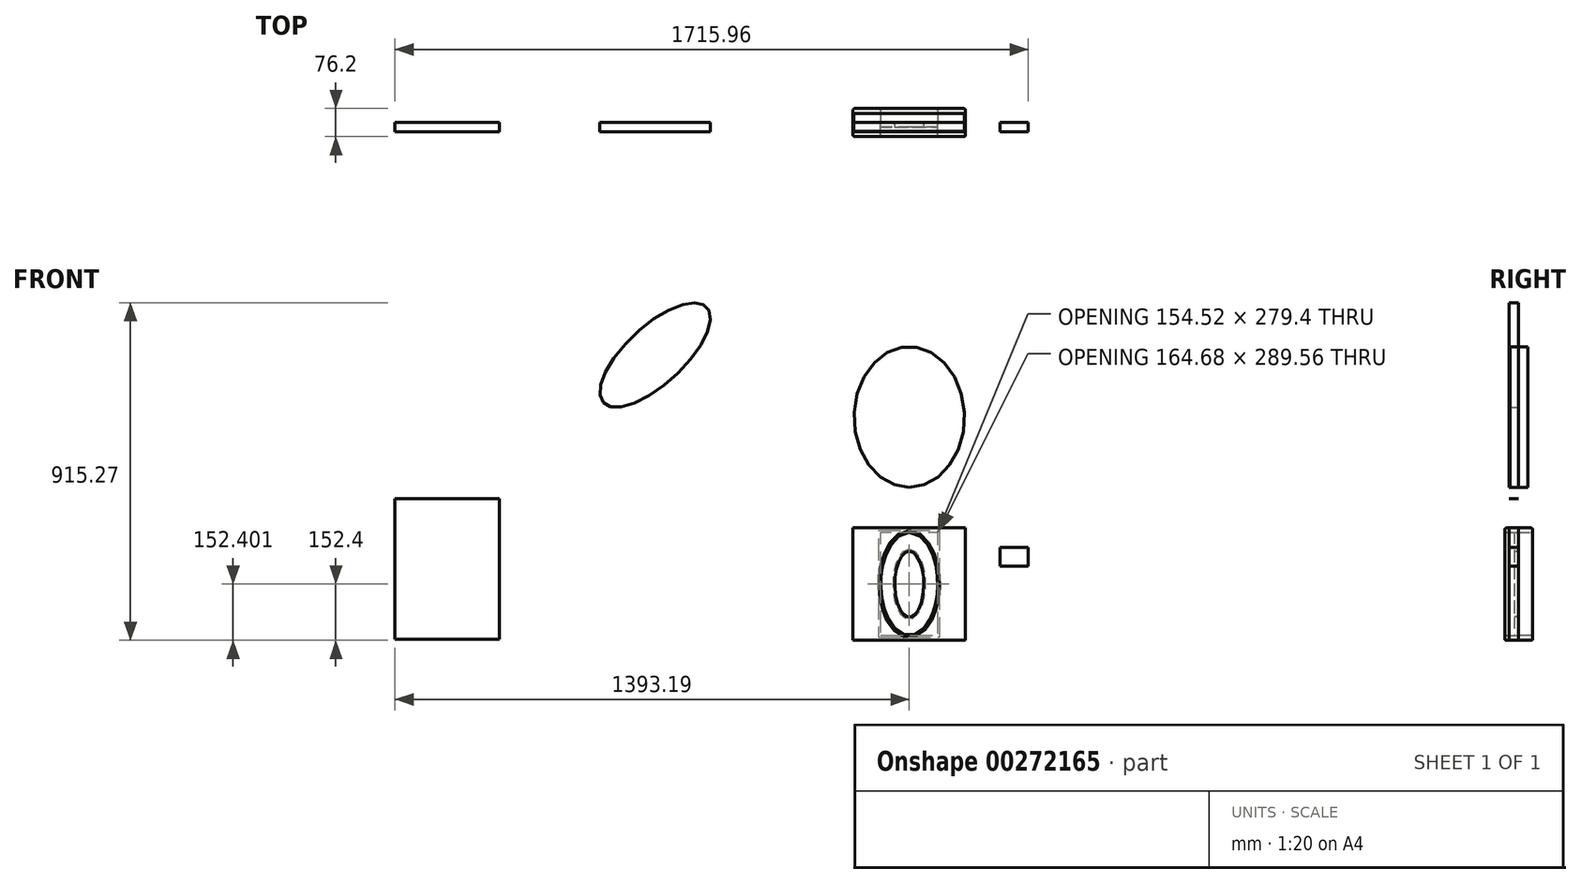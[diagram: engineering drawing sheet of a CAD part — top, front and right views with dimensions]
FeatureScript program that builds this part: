
annotation { "Feature Type Name" : "Feature", "Feature Type Description" : "" }
export const myFeature = defineFeature(function(context is Context, id is Id, definition is map)
    precondition{}
    {
        {
            var Q0;
            Q0=qCreatedBy(makeId("Front.planeOp"),FACE);
            var sketch = newSketch(context, id + "F0", { "sketchPlane" : qUnion([Q0])});
            skEllipse(sketch, "E0", {"center": v(0, 0) * mm, "majorRadius": 88.9 * mm, "minorRadius": 39.2 * mm, "majorAxis": v(0, 1)});
            skEllipse(sketch, "E1", {"center": v(0, 0) * mm, "majorRadius": 139.7 * mm, "minorRadius": 77.26 * mm, "majorAxis": v(0, 1)});
            skLineSegment(sketch, "E2.bottom", {"start": v(152.4, 152.4) * mm, "end": v(-152.4, 152.4) * mm});
            skLineSegment(sketch, "E2.top", {"start": v(152.4, -152.4) * mm, "end": v(-152.4, -152.4) * mm});
            skLineSegment(sketch, "E2.left", {"start": v(152.4, 152.4) * mm, "end": v(152.4, -152.4) * mm});
            skLineSegment(sketch, "E2.right", {"start": v(-152.4, 152.4) * mm, "end": v(-152.4, -152.4) * mm});
            skEllipse(sketch, "E3", {"center": v(0, 452.6) * mm, "majorRadius": 190.5 * mm, "minorRadius": 149.6 * mm, "majorAxis": v(0, -1)});
            skLineSegment(sketch, "E4.bottom", {"start": v(-269.23, 148.3) * mm, "end": v(-624.83, 148.3) * mm});
            skLineSegment(sketch, "E4.top", {"start": v(-269.23, -207.3) * mm, "end": v(-624.83, -207.3) * mm});
            skLineSegment(sketch, "E4.left", {"start": v(-269.23, 148.3) * mm, "end": v(-269.23, -207.3) * mm});
            skLineSegment(sketch, "E4.right", {"start": v(-624.83, 148.3) * mm, "end": v(-624.83, -207.3) * mm});
            skPoint(sketch, "E4.middle", {"position": v(-447.03, -29.5) * mm});
            skLineSegment(sketch, "E5", {"start": v(246.57, 99.69) * mm, "end": v(246.57, 48.89) * mm});
            skLineSegment(sketch, "E6", {"start": v(246.57, 48.89) * mm, "end": v(322.77, 48.89) * mm});
            skLineSegment(sketch, "E7", {"start": v(322.77, 48.89) * mm, "end": v(322.77, 99.69) * mm});
            skLineSegment(sketch, "E8", {"start": v(322.77, 99.69) * mm, "end": v(246.57, 99.69) * mm});
            skEllipse(sketch, "E9", {"center": v(-688.73, 621.2) * mm, "majorRadius": 190.5 * mm, "minorRadius": 78.41 * mm, "majorAxis": v(-0.73, -0.68)});
            skLineSegment(sketch, "E10.bottom", {"start": v(-1110.18, -149.54) * mm, "end": v(-1393.2, -149.54) * mm});
            skLineSegment(sketch, "E10.top", {"start": v(-1110.18, 231.46) * mm, "end": v(-1393.2, 231.46) * mm});
            skLineSegment(sketch, "E10.left", {"start": v(-1110.18, -149.54) * mm, "end": v(-1110.18, 231.46) * mm});
            skLineSegment(sketch, "E10.right", {"start": v(-1393.2, -149.54) * mm, "end": v(-1393.2, 231.46) * mm});
            skPoint(sketch, "E10.middle", {"position": v(-1251.68, 40.96) * mm});
            skSolve(sketch);
        }
        {
            var Q0;
            Q0=makeQuery(id+"F0.imprint","IMPRINT",FACE,{"disambiguationData":[TD([[makeQuery(id+"F0.imprint","IMPRINT",EDGE,{"derivedFrom":sQuery(id+"F0.wireOp",EDGE,"E1")}),-1.0]])]});
            extrude(context, id + "F1", {"entities" : qUnion([Q0]), "endBound" : BoundingType.SYMMETRIC, "depth" : 76.2 * mm});
        }
        {
            var Q0;
            Q0=makeQuery(id+"F0.imprint","IMPRINT",FACE,{"disambiguationData":[TD([[makeQuery(id+"F0.imprint","IMPRINT",EDGE,{"derivedFrom":sQuery(id+"F0.wireOp",EDGE,"E3")}),1.0]])]});
            extrude(context, id + "F2", {"entities" : qUnion([Q0]), "endBound" : BoundingType.SYMMETRIC, "depth" : 48.26 * mm});
        }
        {
            var Q0;
            Q0=makeQuery(id+"F0.imprint","IMPRINT",FACE,{"disambiguationData":[TD([[makeQuery(id+"F0.imprint","IMPRINT",EDGE,{"derivedFrom":sQuery(id+"F0.wireOp",EDGE,"E0")}),-1.0]])]});
            extrude(context, id + "F3", {"entities" : qUnion([Q0]), "operationType" : NewBodyOperationType.ADD, "depth" : 12.7 * mm});
        }
        {
            var Q0;
            Q0=makeQuery(id+"F1.opExtrude","CAP_FACE",FACE,{"disambiguationData":[OSD([sQuery(id+"F0.wireOp",EDGE,"E1"),sQuery(id+"F0.wireOp",EDGE,"E2.bottom"),sQuery(id+"F0.wireOp",EDGE,"E2.top"),sQuery(id+"F0.wireOp",EDGE,"E2.left"),sQuery(id+"F0.wireOp",EDGE,"E2.right")])],"isStart":false});
            var Q1;
            Q1=makeQuery(id+"F1.opExtrude","SWEPT_EDGE",EDGE,{"disambiguationData":[OSD([sQuery(id+"F0.wireOp",EDGE,"E2.bottom"),sQuery(id+"F0.wireOp",EDGE,"E2.right")])]});
            var Q2;
            Q2=makeQuery(id+"F1.opExtrude","SWEPT_FACE",FACE,{"disambiguationData":[OSD([sQuery(id+"F0.wireOp",EDGE,"E2.bottom")])]});
            var Q3;
            Q3=makeQuery(id+"F1.opExtrude","CAP_EDGE",EDGE,{"disambiguationData":[OSD([sQuery(id+"F0.wireOp",EDGE,"E2.right")])],"isStart":true});
            var Q4;
            Q4=makeQuery(id+"F1.opExtrude","SWEPT_FACE",FACE,{"disambiguationData":[OSD([sQuery(id+"F0.wireOp",EDGE,"E2.top")])]});
            var Q5;
            Q5=makeQuery(id+"F1.opExtrude","CAP_FACE",FACE,{"disambiguationData":[OSD([sQuery(id+"F0.wireOp",EDGE,"E1"),sQuery(id+"F0.wireOp",EDGE,"E2.bottom"),sQuery(id+"F0.wireOp",EDGE,"E2.top"),sQuery(id+"F0.wireOp",EDGE,"E2.left"),sQuery(id+"F0.wireOp",EDGE,"E2.right")])],"isStart":true});
            fillet(context, id + "F4", {"entities" : qUnion([Q0, Q1, Q2, Q3, Q4, Q5]), "radius" : 5.08 * mm, "tangentPropagation" : true, "allowEdgeOverflow" : false});
        }
        {
            var Q0;
            Q0=makeQuery(id+"F3.opExtrude","CAP_EDGE",EDGE,{"disambiguationData":[OSD([sQuery(id+"F0.wireOp",EDGE,"E0")])],"isStart":true});
            fillet(context, id + "F5", {"entities" : qUnion([Q0]), "radius" : 5.08 * mm, "tangentPropagation" : true, "allowEdgeOverflow" : false});
        }
        {
            var Q0;
            Q0 = qSketchRegion(id + "F0", true);
            extrude(context, id + "F6", {"entities" : qUnion([Q0]), "depth" : 25.4 * mm});
        }
        {
            var Q0;
            Q0=makeQuery(id+"F6.opExtrude","SWEPT_BODY",BODY,{"disambiguationData":[OSD([sQuery(id+"F0.wireOp",EDGE,"E4.bottom"),sQuery(id+"F0.wireOp",EDGE,"E4.top"),sQuery(id+"F0.wireOp",EDGE,"E4.left"),sQuery(id+"F0.wireOp",EDGE,"E4.right")])]});
            deleteBodies(context, id + "F7", {"entities" : qUnion([Q0])});
        }
    });
